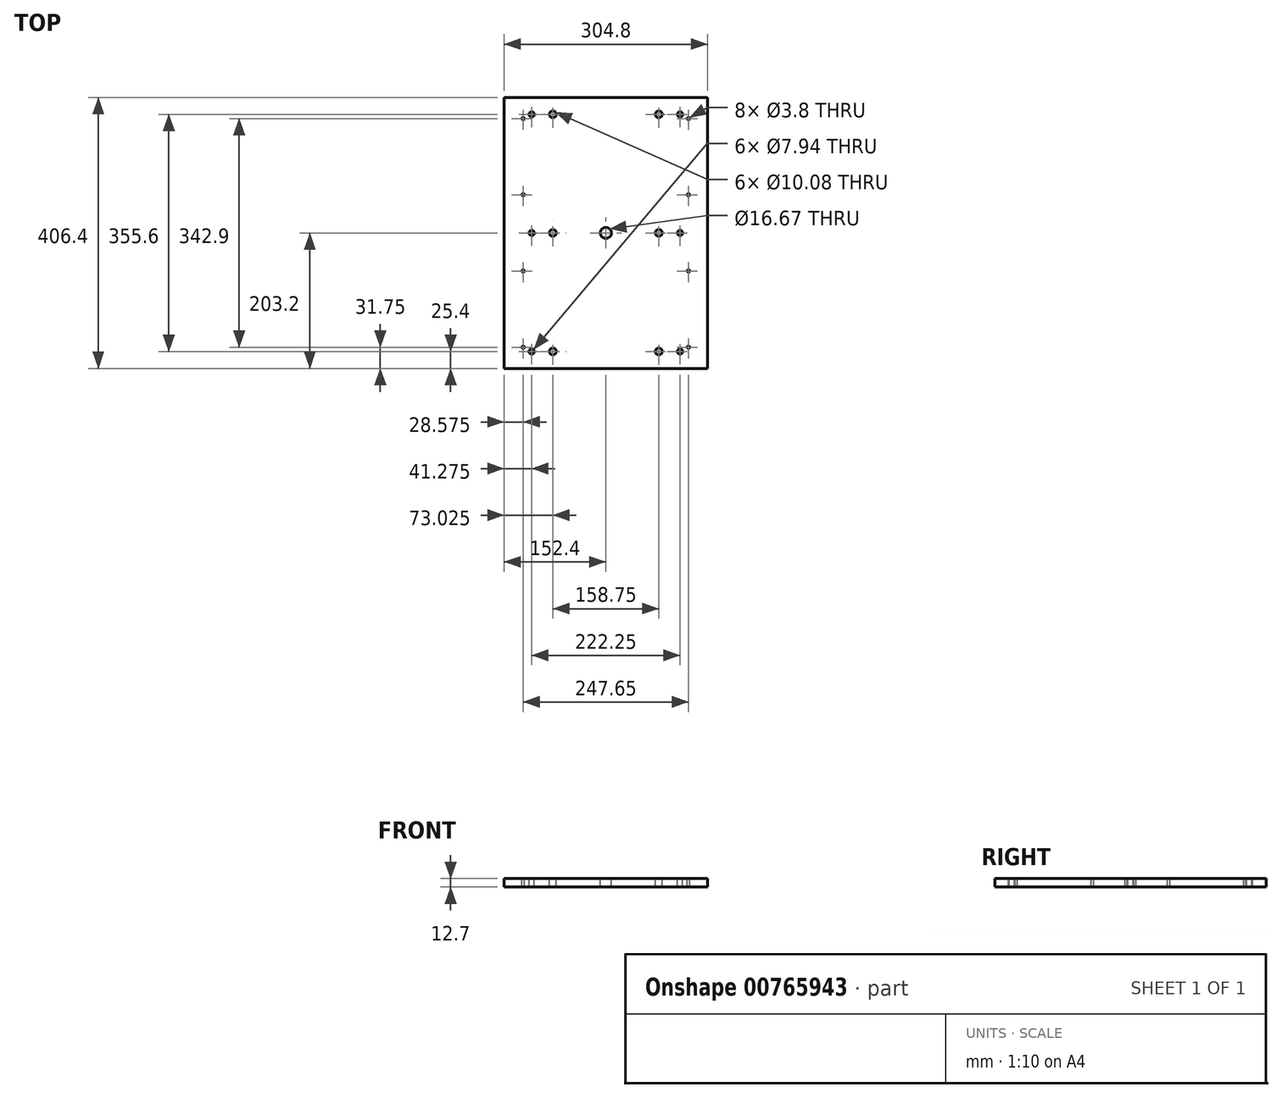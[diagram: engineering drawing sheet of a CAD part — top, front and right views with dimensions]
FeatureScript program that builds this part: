
annotation { "Feature Type Name" : "Feature", "Feature Type Description" : "" }
export const myFeature = defineFeature(function(context is Context, id is Id, definition is map)
    precondition{}
    {
        {
            var Q0;
            Q0=qCreatedBy(makeId("Front.planeOp"),FACE);
            var sketch = newSketch(context, id + "F0", { "sketchPlane" : qUnion([Q0])});
            skLineSegment(sketch, "E0.bottom", {"start": v(0, 0) * mm, "end": v(304.8, 0) * mm});
            skLineSegment(sketch, "E0.top", {"start": v(0, 12.7) * mm, "end": v(304.8, 12.7) * mm});
            skLineSegment(sketch, "E0.left", {"start": v(0, 0) * mm, "end": v(0, 12.7) * mm});
            skLineSegment(sketch, "E0.right", {"start": v(304.8, 0) * mm, "end": v(304.8, 12.7) * mm});
            skSolve(sketch);
        }
        {
            var Q0;
            Q0 = qSketchRegion(id + "F0", true);
            extrude(context, id + "F1", {"entities" : qUnion([Q0]), "depth" : 406.4 * mm, "offsetDistance" : 25.4 * mm});
        }
        {
            var Q0;
            Q0=makeQuery(id+"F1.opExtrude","SWEPT_FACE",FACE,{"disambiguationData":[OSD([sQuery(id+"F0.wireOp",EDGE,"E0.top")])]});
            var sketch = newSketch(context, id + "F2", { "sketchPlane" : qUnion([Q0])});
            skLineSegment(sketch, "E1", {"start": v(152.4, 0) * mm, "end": v(152.4, -406.4) * mm, "construction": true});
            skLineSegment(sketch, "E2", {"start": v(263.53, 0) * mm, "end": v(263.53, -406.4) * mm, "construction": true});
            skLineSegment(sketch, "E3", {"start": v(231.77, 0) * mm, "end": v(231.78, -406.4) * mm, "construction": true});
            skPoint(sketch, "E4", {"position": v(263.53, -381) * mm});
            skPoint(sketch, "E5", {"position": v(263.53, -203.2) * mm});
            skPoint(sketch, "E6", {"position": v(263.53, -25.4) * mm});
            skPoint(sketch, "E7", {"position": v(231.78, -381) * mm});
            skPoint(sketch, "E8", {"position": v(231.78, -203.2) * mm});
            skPoint(sketch, "E9", {"position": v(231.77, -25.4) * mm});
            skPoint(sketch, "E10.MirrorP", {"position": v(73.03, -381) * mm});
            skPoint(sketch, "E11.MirrorP", {"position": v(73.03, -203.2) * mm});
            skPoint(sketch, "E12.MirrorP", {"position": v(41.28, -203.2) * mm});
            skPoint(sketch, "E13.MirrorP", {"position": v(41.28, -381) * mm});
            skPoint(sketch, "E14.MirrorP", {"position": v(73.03, -25.4) * mm});
            skPoint(sketch, "E15.MirrorP", {"position": v(41.28, -25.4) * mm});
            skPoint(sketch, "E16", {"position": v(152.4, -203.2) * mm});
            skLineSegment(sketch, "E17", {"start": v(241.3, 0) * mm, "end": v(241.3, -83.01) * mm, "construction": true});
            skLineSegment(sketch, "E18", {"start": v(254, -406.4) * mm, "end": v(254, -289.58) * mm, "construction": true});
            skLineSegment(sketch, "E19.MirrorCS", {"start": v(50.8, -406.4) * mm, "end": v(50.8, -289.58) * mm, "construction": true});
            skSolve(sketch);
        }
        {
            var Q0;
            Q0=sQuery(id+"F2.wireOp",VERTEX,"E13.MirrorP");
            var Q1;
            Q1=sQuery(id+"F2.wireOp",VERTEX,"E12.MirrorP");
            var Q2;
            Q2=sQuery(id+"F2.wireOp",VERTEX,"E15.MirrorP");
            var Q3;
            Q3=sQuery(id+"F2.wireOp",VERTEX,"E6");
            var Q4;
            Q4=sQuery(id+"F2.wireOp",VERTEX,"E5");
            var Q5;
            Q5=sQuery(id+"F2.wireOp",VERTEX,"E4");
            var Q6;
            Q6=makeQuery(id+"F1.opExtrude","SWEPT_BODY",BODY,{"disambiguationData":[OSD([sQuery(id+"F0.wireOp",EDGE,"E0.bottom"),sQuery(id+"F0.wireOp",EDGE,"E0.top"),sQuery(id+"F0.wireOp",EDGE,"E0.left"),sQuery(id+"F0.wireOp",EDGE,"E0.right")])]});
            hole(context, id + "F3", {"style" : HoleStyle.SIMPLE, "endStyle" : HoleEndStyle.BLIND, "standardTappedOrClearance" : lookupTablePath({ "standard" : "ANSI", "engagement" : "75%", "pitch" : "16 tpi", "size" : "3/8", "type" : "Tapped" }), "standardBlindInLast" : lookupTablePath({ "standard" : "ANSI", "engagement" : "75%", "pitch" : "16 tpi", "size" : "3/8", "type" : "Tapped" }), "holeDiameter" : 7.94 * mm, "majorDiameter" : 9.52 * mm, "showTappedDepth" : true, "holeDepth" : 20.66 * mm, "isTappedThrough" : true, "tappedDepth" : 15.9 * mm, "tapClearance" : 3, "locations" : qUnion([Q0, Q1, Q2, Q3, Q4, Q5]), "scope" : qUnion([Q6])});
        }
        {
            var Q0;
            Q0=sQuery(id+"F2.wireOp",VERTEX,"E10.MirrorP");
            var Q1;
            Q1=sQuery(id+"F2.wireOp",VERTEX,"E11.MirrorP");
            var Q2;
            Q2=sQuery(id+"F2.wireOp",VERTEX,"E14.MirrorP");
            var Q3;
            Q3=sQuery(id+"F2.wireOp",VERTEX,"E7");
            var Q4;
            Q4=sQuery(id+"F2.wireOp",VERTEX,"E8");
            var Q5;
            Q5=sQuery(id+"F2.wireOp",VERTEX,"E9");
            var Q6;
            Q6=makeQuery(id+"F1.opExtrude","SWEPT_BODY",BODY,{"disambiguationData":[OSD([sQuery(id+"F0.wireOp",EDGE,"E0.bottom"),sQuery(id+"F0.wireOp",EDGE,"E0.top"),sQuery(id+"F0.wireOp",EDGE,"E0.left"),sQuery(id+"F0.wireOp",EDGE,"E0.right")])]});
            hole(context, id + "F4", {"style" : HoleStyle.SIMPLE, "endStyle" : HoleEndStyle.BLIND, "standardTappedOrClearance" : lookupTablePath({ "standard" : "ANSI", "fit" : "Normal (ASME)", "size" : "3/8", "type" : "Clearance" }), "standardBlindInLast" : lookupTablePath({ "fit" : "Free", "standard" : "ANSI", "size" : "3/8", "type" : "Clearance" }), "holeDiameter" : 10.08 * mm, "majorDiameter" : 9.52 * mm, "holeDepth" : 20.68 * mm, "isTappedThrough" : true, "tappedDepth" : 15.9 * mm, "tapClearance" : 3, "locations" : qUnion([Q0, Q1, Q2, Q3, Q4, Q5]), "scope" : qUnion([Q6])});
        }
        {
            var Q0;
            Q0=sQuery(id+"F2.wireOp",VERTEX,"E16");
            var Q1;
            Q1=makeQuery(id+"F1.opExtrude","SWEPT_BODY",BODY,{"disambiguationData":[OSD([sQuery(id+"F0.wireOp",EDGE,"E0.bottom"),sQuery(id+"F0.wireOp",EDGE,"E0.top"),sQuery(id+"F0.wireOp",EDGE,"E0.left"),sQuery(id+"F0.wireOp",EDGE,"E0.right")])]});
            hole(context, id + "F5", {"style" : HoleStyle.SIMPLE, "endStyle" : HoleEndStyle.BLIND, "standardTappedOrClearance" : lookupTablePath({ "standard" : "ANSI", "fit" : "Normal (ASME)", "size" : "5/8", "type" : "Clearance" }), "standardBlindInLast" : lookupTablePath({ "fit" : "Free", "standard" : "ANSI", "size" : "5/8", "type" : "Clearance" }), "holeDiameter" : 16.67 * mm, "majorDiameter" : 4.83 * mm, "holeDepth" : 19.1 * mm, "isTappedThrough" : true, "tappedDepth" : 15.93 * mm, "tapClearance" : 3, "locations" : qUnion([Q0]), "scope" : qUnion([Q1])});
        }
        {
            var Q0;
            {var subQ0=sQuery(id+"F0.wireOp",EDGE,"E0.top");Q0=makeQuery(id+"F2.imprint","IMPRINT",FACE,{"disambiguationData":[TD([[makeQuery(id+"F2.imprint","IMPRINT",EDGE,{"derivedFrom":makeQuery(id+"F1.opExtrude","CAP_EDGE",EDGE,{"disambiguationData":[OSD([subQ0])],"isStart":true})}),-1.0]])]});}
            var sketch = newSketch(context, id + "F6", { "sketchPlane" : qUnion([Q0])});
            skLineSegment(sketch, "E20", {"start": v(276.23, 0) * mm, "end": v(276.23, -636.8) * mm, "construction": true});
            skPoint(sketch, "E21", {"position": v(276.22, -31.75) * mm});
            skPoint(sketch, "E22", {"position": v(276.23, -146.05) * mm});
            skPoint(sketch, "E23", {"position": v(276.23, -260.35) * mm});
            skPoint(sketch, "E24", {"position": v(276.23, -374.65) * mm});
            skPoint(sketch, "E25.MirrorP", {"position": v(28.58, -31.75) * mm});
            skPoint(sketch, "E26.MirrorP", {"position": v(28.58, -146.05) * mm});
            skPoint(sketch, "E27.MirrorP", {"position": v(28.58, -260.35) * mm});
            skPoint(sketch, "E28.MirrorP", {"position": v(28.58, -374.65) * mm});
            skSolve(sketch);
        }
        {
            var Q0;
            Q0=sQuery(id+"F6.wireOp",VERTEX,"E25.MirrorP");
            var Q1;
            Q1=sQuery(id+"F6.wireOp",VERTEX,"E21");
            var Q2;
            Q2=sQuery(id+"F6.wireOp",VERTEX,"E22");
            var Q3;
            Q3=sQuery(id+"F6.wireOp",VERTEX,"E23");
            var Q4;
            Q4=sQuery(id+"F6.wireOp",VERTEX,"E24");
            var Q5;
            Q5=sQuery(id+"F6.wireOp",VERTEX,"E28.MirrorP");
            var Q6;
            Q6=sQuery(id+"F6.wireOp",VERTEX,"E27.MirrorP");
            var Q7;
            Q7=sQuery(id+"F6.wireOp",VERTEX,"E26.MirrorP");
            var Q8;
            Q8=makeQuery(id+"F1.opExtrude","SWEPT_BODY",BODY,{"disambiguationData":[OSD([sQuery(id+"F0.wireOp",EDGE,"E0.bottom"),sQuery(id+"F0.wireOp",EDGE,"E0.top"),sQuery(id+"F0.wireOp",EDGE,"E0.left"),sQuery(id+"F0.wireOp",EDGE,"E0.right")])]});
            hole(context, id + "F7", {"style" : HoleStyle.SIMPLE, "endStyle" : HoleEndStyle.BLIND, "standardTappedOrClearance" : lookupTablePath({ "standard" : "ANSI", "engagement" : "75%", "pitch" : "24 tpi", "size" : "#10", "type" : "Tapped" }), "standardBlindInLast" : lookupTablePath({ "standard" : "ANSI", "engagement" : "75%", "pitch" : "24 tpi", "size" : "#10", "type" : "Tapped" }), "holeDiameter" : 3.8 * mm, "majorDiameter" : 4.83 * mm, "showTappedDepth" : true, "holeDepth" : 19.1 * mm, "isTappedThrough" : true, "tappedDepth" : 15.93 * mm, "tapClearance" : 3, "locations" : qUnion([Q0, Q1, Q2, Q3, Q4, Q5, Q6, Q7]), "scope" : qUnion([Q8])});
        }
    });
